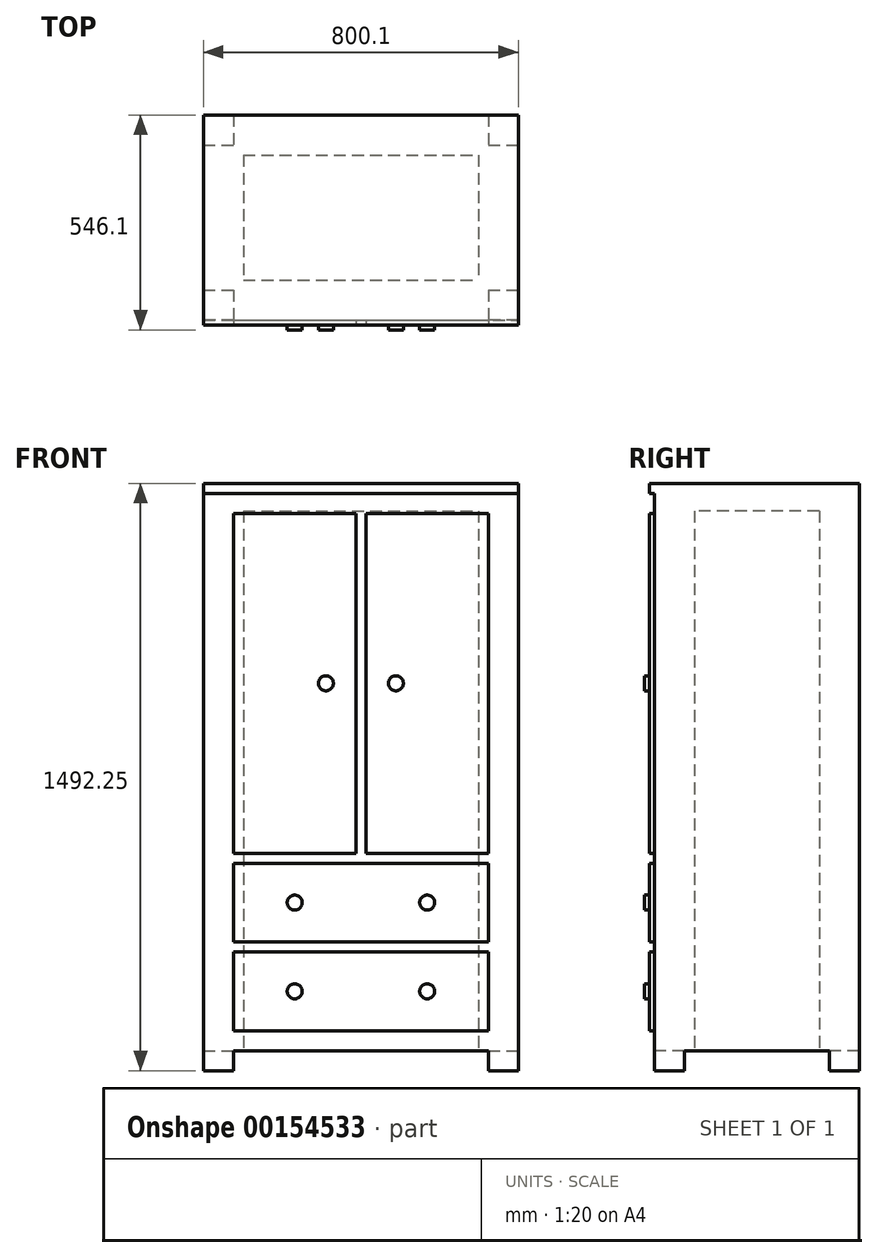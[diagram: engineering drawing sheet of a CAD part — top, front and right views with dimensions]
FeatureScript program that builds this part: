
annotation { "Feature Type Name" : "Feature", "Feature Type Description" : "" }
export const myFeature = defineFeature(function(context is Context, id is Id, definition is map)
    precondition{}
    {
        {
            var Q0;
            Q0=qCreatedBy(makeId("Top.planeOp"),FACE);
            var sketch = newSketch(context, id + "F0", { "sketchPlane" : qUnion([Q0])});
            skLineSegment(sketch, "E0.bottom", {"start": v(400.05, 266.7) * mm, "end": v(-400.05, 266.7) * mm});
            skLineSegment(sketch, "E0.top", {"start": v(400.05, -266.7) * mm, "end": v(-400.05, -266.7) * mm});
            skLineSegment(sketch, "E0.left", {"start": v(400.05, 266.7) * mm, "end": v(400.05, -266.7) * mm});
            skLineSegment(sketch, "E0.right", {"start": v(-400.05, 266.7) * mm, "end": v(-400.05, -266.7) * mm});
            skPoint(sketch, "E0.middle", {"position": v(0, 0) * mm});
            skSolve(sketch);
        }
        {
            var Q0;
            Q0=makeQuery(id+"F0.imprint","IMPRINT",FACE,{"disambiguationData":[TD([[makeQuery(id+"F0.imprint","IMPRINT",EDGE,{"derivedFrom":sQuery(id+"F0.wireOp",EDGE,"E0.bottom")}),1.0]])]});
            extrude(context, id + "F1", {"entities" : qUnion([Q0]), "depth" : 1492.25 * mm});
        }
        {
            var Q0;
            Q0=makeQuery(id+"F1.opExtrude","SWEPT_FACE",FACE,{"disambiguationData":[OSD([sQuery(id+"F0.wireOp",EDGE,"E0.top")])]});
            var sketch = newSketch(context, id + "F2", { "sketchPlane" : qUnion([Q0])});
            skLineSegment(sketch, "E1.bottom", {"start": v(-323.85, 0) * mm, "end": v(323.85, 0) * mm});
            skLineSegment(sketch, "E1.top", {"start": v(-323.85, 50.8) * mm, "end": v(323.85, 50.8) * mm});
            skLineSegment(sketch, "E1.left", {"start": v(-323.85, 0) * mm, "end": v(-323.85, 50.8) * mm});
            skLineSegment(sketch, "E1.right", {"start": v(323.85, 0) * mm, "end": v(323.85, 50.8) * mm});
            skLineSegment(sketch, "E2.bottom", {"start": v(-323.85, 101.6) * mm, "end": v(323.85, 101.6) * mm});
            skLineSegment(sketch, "E2.top", {"start": v(-323.85, 301.63) * mm, "end": v(323.85, 301.63) * mm});
            skLineSegment(sketch, "E2.left", {"start": v(-323.85, 101.6) * mm, "end": v(-323.85, 301.63) * mm});
            skLineSegment(sketch, "E2.right", {"start": v(323.85, 101.6) * mm, "end": v(323.85, 301.63) * mm});
            skLineSegment(sketch, "E3.bottom", {"start": v(323.85, 327.03) * mm, "end": v(-323.85, 327.03) * mm});
            skLineSegment(sketch, "E3.top", {"start": v(323.85, 527.05) * mm, "end": v(-323.85, 527.05) * mm});
            skLineSegment(sketch, "E3.left", {"start": v(323.85, 327.03) * mm, "end": v(323.85, 527.05) * mm});
            skLineSegment(sketch, "E3.right", {"start": v(-323.85, 327.03) * mm, "end": v(-323.85, 527.05) * mm});
            skLineSegment(sketch, "E4.bottom", {"start": v(-323.85, 1416.05) * mm, "end": v(-12.7, 1416.05) * mm});
            skLineSegment(sketch, "E4.top", {"start": v(-323.85, 552.45) * mm, "end": v(-12.7, 552.45) * mm});
            skLineSegment(sketch, "E4.left", {"start": v(-323.85, 1416.05) * mm, "end": v(-323.85, 552.45) * mm});
            skLineSegment(sketch, "E4.right", {"start": v(-12.7, 1416.05) * mm, "end": v(-12.7, 552.45) * mm});
            skLineSegment(sketch, "E5.bottom", {"start": v(12.7, 1416.05) * mm, "end": v(323.85, 1416.05) * mm});
            skLineSegment(sketch, "E5.top", {"start": v(12.7, 552.45) * mm, "end": v(323.85, 552.45) * mm});
            skLineSegment(sketch, "E5.left", {"start": v(12.7, 1416.05) * mm, "end": v(12.7, 552.45) * mm});
            skLineSegment(sketch, "E5.right", {"start": v(323.85, 1416.05) * mm, "end": v(323.85, 552.45) * mm});
            skLineSegment(sketch, "E6.bottom", {"start": v(-400.05, 1492.25) * mm, "end": v(400.05, 1492.25) * mm});
            skLineSegment(sketch, "E6.top", {"start": v(-400.05, 1466.85) * mm, "end": v(400.05, 1466.85) * mm});
            skLineSegment(sketch, "E6.left", {"start": v(-400.05, 1492.25) * mm, "end": v(-400.05, 1466.85) * mm});
            skLineSegment(sketch, "E6.right", {"start": v(400.05, 1492.25) * mm, "end": v(400.05, 1466.85) * mm});
            skSolve(sketch);
        }
        {
            var Q0;
            Q0=makeQuery(id+"F2.imprint","IMPRINT",FACE,{"disambiguationData":[TD([[makeQuery(id+"F2.imprint","IMPRINT",EDGE,{"derivedFrom":sQuery(id+"F2.wireOp",EDGE,"E1.top")}),1.0]])]});
            extrude(context, id + "F3", {"entities" : qUnion([Q0]), "operationType" : NewBodyOperationType.REMOVE, "oppositeDirection" : true, "depth" : 12.7 * mm});
        }
        {
            var Q0;
            Q0=makeQuery(id+"F2.imprint","IMPRINT",FACE,{"disambiguationData":[TD([[makeQuery(id+"F2.imprint","IMPRINT",EDGE,{"derivedFrom":sQuery(id+"F2.wireOp",EDGE,"E1.bottom")}),-1.0]])]});
            extrude(context, id + "F4", {"entities" : qUnion([Q0]), "operationType" : NewBodyOperationType.REMOVE, "endBound" : BoundingType.THROUGH_ALL, "oppositeDirection" : true, "depth" : 30.48 * mm});
        }
        {
            var Q0;
            Q0=makeQuery(id+"F1.opExtrude","SWEPT_FACE",FACE,{"disambiguationData":[OSD([sQuery(id+"F0.wireOp",EDGE,"E0.left")])]});
            var sketch = newSketch(context, id + "F5", { "sketchPlane" : qUnion([Q0])});
            skLineSegment(sketch, "E7.bottom", {"start": v(-177.8, 0) * mm, "end": v(190.5, 0) * mm});
            skLineSegment(sketch, "E7.top", {"start": v(-177.8, 50.8) * mm, "end": v(190.5, 50.8) * mm});
            skLineSegment(sketch, "E7.left", {"start": v(-177.8, 0) * mm, "end": v(-177.8, 50.8) * mm});
            skLineSegment(sketch, "E7.right", {"start": v(190.5, 0) * mm, "end": v(190.5, 50.8) * mm});
            skSolve(sketch);
        }
        {
            var Q0;
            Q0 = qSketchRegion(id + "F5", true);
            extrude(context, id + "F6", {"entities" : qUnion([Q0]), "operationType" : NewBodyOperationType.REMOVE, "endBound" : BoundingType.THROUGH_ALL, "oppositeDirection" : true, "depth" : 30.48 * mm});
        }
        {
            var Q0;
            Q0=makeQuery(id+"F6.boolean.opBoolean","MERGE",FACE,{"derivedFrom":[makeQuery(id+"F4.boolean.opBoolean","COPY",FACE,{"derivedFrom":makeQuery(id+"F4.opExtrude","SWEPT_FACE",FACE,{"disambiguationData":[OSD([sQuery(id+"F2.wireOp",EDGE,"E1.top")])]})}),makeQuery(id+"F6.opExtrude","SWEPT_FACE",FACE,{"disambiguationData":[OSD([sQuery(id+"F5.wireOp",EDGE,"E7.top")])]})]});
            var sketch = newSketch(context, id + "F7", { "sketchPlane" : qUnion([Q0])});
            skLineSegment(sketch, "E8.bottom", {"start": v(-298.45, -165.1) * mm, "end": v(298.45, -165.1) * mm});
            skLineSegment(sketch, "E8.top", {"start": v(-298.45, 152.4) * mm, "end": v(298.45, 152.4) * mm});
            skLineSegment(sketch, "E8.left", {"start": v(-298.45, -165.1) * mm, "end": v(-298.45, 152.4) * mm});
            skLineSegment(sketch, "E8.right", {"start": v(298.45, -165.1) * mm, "end": v(298.45, 152.4) * mm});
            skSolve(sketch);
        }
        {
            var Q0;
            Q0 = qSketchRegion(id + "F7", true);
            extrude(context, id + "F8", {"entities" : qUnion([Q0]), "operationType" : NewBodyOperationType.REMOVE, "oppositeDirection" : true, "depth" : 1371.6 * mm});
        }
        {
            var Q0;
            Q0=makeQuery(id+"F3.boolean.opBoolean","SPLIT",FACE,{"disambiguationData":[TD([makeQuery(id+"F3.opExtrude","SWEPT_FACE",FACE,{"disambiguationData":[OSD([sQuery(id+"F2.wireOp",EDGE,"E4.bottom")])]})])],"derivedFrom":makeQuery(id+"F1.opExtrude","SWEPT_FACE",FACE,{"disambiguationData":[OSD([sQuery(id+"F0.wireOp",EDGE,"E0.top")])]})});
            var sketch = newSketch(context, id + "F9", { "sketchPlane" : qUnion([Q0])});
            skCircle(sketch, "E9", {"center": v(-88.9, 984.25) * mm, "radius": 19.05 * mm});
            skCircle(sketch, "E10", {"center": v(88.9, 984.25) * mm, "radius": 19.05 * mm});
            skCircle(sketch, "E11", {"center": v(168.27, 427.04) * mm, "radius": 19.05 * mm});
            skCircle(sketch, "E12", {"center": v(-168.28, 427.04) * mm, "radius": 19.05 * mm});
            skCircle(sketch, "E13", {"center": v(-168.28, 201.61) * mm, "radius": 19.05 * mm});
            skCircle(sketch, "E14", {"center": v(168.27, 201.61) * mm, "radius": 19.05 * mm});
            skLineSegment(sketch, "E15", {"start": v(-12.7, 984.25) * mm, "end": v(-88.9, 984.25) * mm, "construction": true});
            skLineSegment(sketch, "E16", {"start": v(88.9, 984.25) * mm, "end": v(12.7, 984.25) * mm, "construction": true});
            skLineSegment(sketch, "E17.0", {"start": v(12.7, 1416.05) * mm, "end": v(12.7, 552.45) * mm, "construction": true});
            skLineSegment(sketch, "E18.1", {"start": v(-323.85, 327.03) * mm, "end": v(-323.85, 527.05) * mm, "construction": true});
            skLineSegment(sketch, "E19.0.0", {"start": v(-323.85, 301.63) * mm, "end": v(-323.85, 101.6) * mm, "construction": true});
            skLineSegment(sketch, "E19.0.1", {"start": v(-323.85, 101.6) * mm, "end": v(323.85, 101.6) * mm});
            skLineSegment(sketch, "E19.0.2", {"start": v(323.85, 101.6) * mm, "end": v(323.85, 301.63) * mm});
            skLineSegment(sketch, "E19.0.3", {"start": v(323.85, 301.63) * mm, "end": v(-323.85, 301.63) * mm, "construction": true});
            skLineSegment(sketch, "E19.1", {"start": v(-323.85, 101.6) * mm, "end": v(-323.85, 301.63) * mm});
            skLineSegment(sketch, "E20.0", {"start": v(323.85, 527.05) * mm, "end": v(-323.85, 527.05) * mm, "construction": true});
            skLineSegment(sketch, "E21", {"start": v(-168.28, 427.04) * mm, "end": v(-323.85, 427.04) * mm, "construction": true});
            skLineSegment(sketch, "E22", {"start": v(-323.85, 201.61) * mm, "end": v(-168.28, 201.61) * mm, "construction": true});
            skLineSegment(sketch, "E23.0", {"start": v(-323.85, 552.45) * mm, "end": v(-12.7, 552.45) * mm, "construction": true});
            skLineSegment(sketch, "E24.0", {"start": v(12.7, 552.45) * mm, "end": v(323.85, 552.45) * mm, "construction": true});
            skLineSegment(sketch, "E25", {"start": v(-168.28, 427.04) * mm, "end": v(-168.28, 552.45) * mm, "construction": true});
            skLineSegment(sketch, "E26", {"start": v(168.27, 427.04) * mm, "end": v(168.27, 552.45) * mm, "construction": true});
            skSolve(sketch);
        }
        {
            var Q0;
            Q0 = qSketchRegion(id + "F9", true);
            extrude(context, id + "F10", {"entities" : qUnion([Q0]), "operationType" : NewBodyOperationType.ADD, "depth" : 12.7 * mm});
        }
    });
